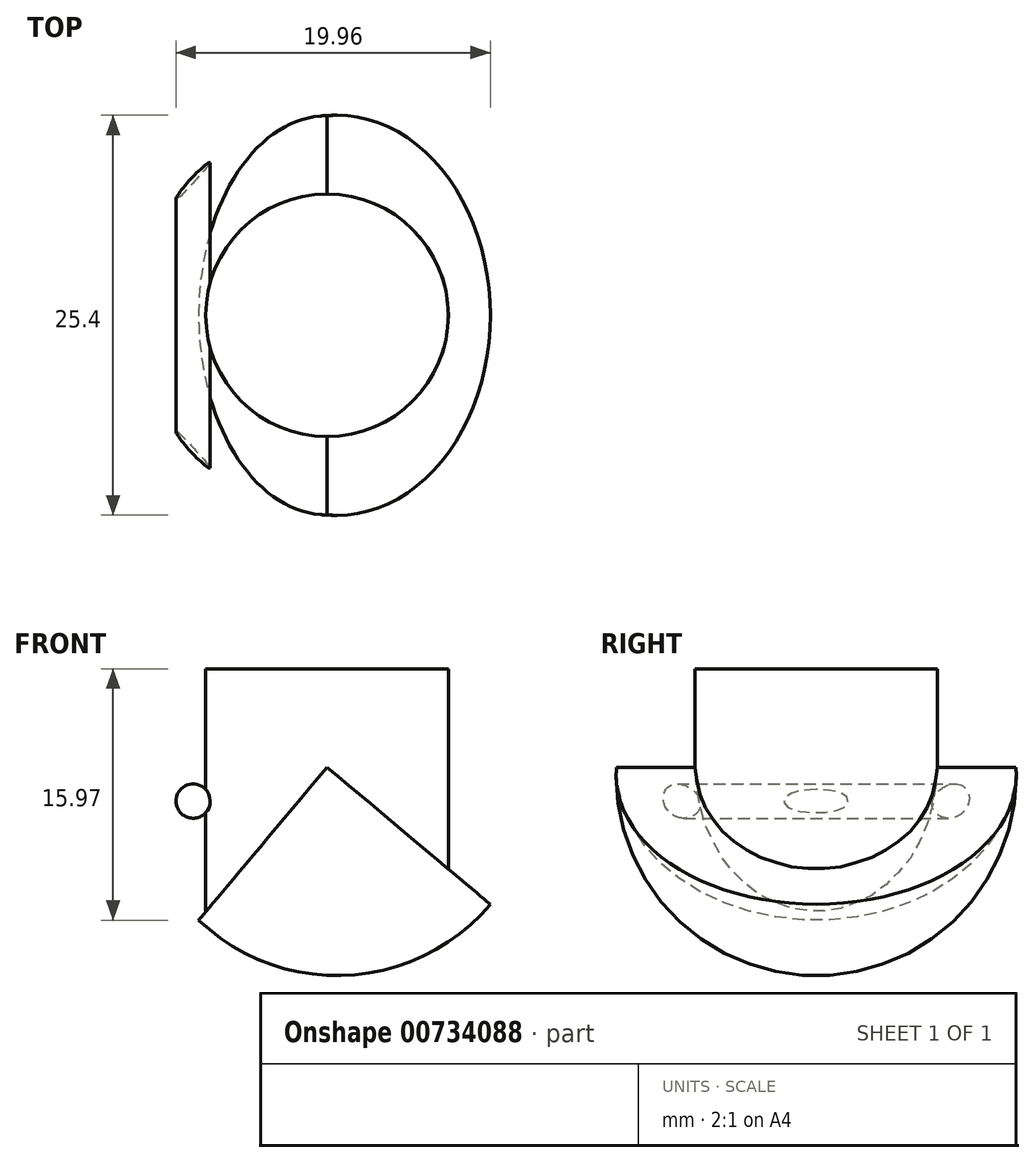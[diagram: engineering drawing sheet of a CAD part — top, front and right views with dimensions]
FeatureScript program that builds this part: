
annotation { "Feature Type Name" : "Feature", "Feature Type Description" : "" }
export const myFeature = defineFeature(function(context is Context, id is Id, definition is map)
    precondition{}
    {
        {
            var Q0;
            Q0=qCreatedBy(makeId("Top.planeOp"),FACE);
            var sketch = newSketch(context, id + "F0", { "sketchPlane" : qUnion([Q0])});
            skCircle(sketch, "E0", {"center": v(0, 0) * mm, "radius": 5.5 * mm});
            skSolve(sketch);
        }
        {
            var Q0;
            Q0=makeQuery(id+"F0.imprint","IMPRINT",FACE,{"disambiguationData":[TD([[makeQuery(id+"F0.imprint","IMPRINT",EDGE,{"derivedFrom":sQuery(id+"F0.wireOp",EDGE,"E0")}),1.0]])]});
            extrude(context, id + "F1", {"entities" : qUnion([Q0]), "depth" : 150 * mm, "offsetDistance" : 25 * mm});
        }
        {
            var Q0;
            Q0=makeQuery(id+"F1.opExtrude","CAP_FACE",FACE,{"disambiguationData":[OSD([sQuery(id+"F0.wireOp",EDGE,"E0")])],"isStart":false});
            var sketch = newSketch(context, id + "F2", { "sketchPlane" : qUnion([Q0])});
            skArc(sketch, "E1", {"start": v(-49.75, 2.8) * mm, "mid": v(-66.59, 8.91) * mm, "end": v(-77.27, -5.46) * mm});
            skLineSegment(sketch, "E2", {"start": v(-49.75, 2.8) * mm, "end": v(-59.49, -5.4) * mm});
            skPoint(sketch, "E3.orphan", {"position": v(-47.27, -5.46) * mm});
            skCircle(sketch, "E4", {"center": v(-60.28, 5.16) * mm, "radius": 2 * mm});
            skLineSegment(sketch, "E5", {"start": v(-53.08, 0) * mm, "end": v(-41.16, 0) * mm});
            skLineSegment(sketch, "E6.MirrorCS", {"start": v(-53.05, -10.77) * mm, "end": v(-41.13, -10.7) * mm});
            skLineSegment(sketch, "E7.MirrorCS", {"start": v(-49.7, -13.56) * mm, "end": v(-59.49, -5.4) * mm});
            skArc(sketch, "E8.MirrorCS", {"start": v(-49.7, -13.56) * mm, "mid": v(-66.5, -19.76) * mm, "end": v(-77.27, -5.46) * mm});
            skSolve(sketch);
        }
        {
            var Q0;
            Q0 = qSketchRegion(id + "F2", true);
            extrude(context, id + "F3", {"entities" : qUnion([Q0]), "depth" : 7 * mm, "offsetDistance" : 25 * mm});
        }
        {
            var Q0;
            Q0=qCreatedBy(makeId("Right.planeOp"),FACE);
            var sketch = newSketch(context, id + "F4", { "sketchPlane" : qUnion([Q0])});
            skLineSegment(sketch, "E9", {"start": v(0, 180.23) * mm, "end": v(0, 162.06) * mm});
            skArc(sketch, "E10", {"start": v(0, 162.06) * mm, "mid": v(9.07, 171.14) * mm, "end": v(0, 180.23) * mm});
            skSolve(sketch);
        }
        {
            var Q0;
            Q0=makeQuery(id+"F4.imprint","IMPRINT",FACE,{"disambiguationData":[TD([[makeQuery(id+"F4.imprint","IMPRINT",EDGE,{"derivedFrom":sQuery(id+"F4.wireOp",EDGE,"E9")}),1.0]])]});
            var Q1;
            Q1=sQuery(id+"F4.wireOp",EDGE,"E9");
            revolve(context, id + "F5", {"surfaceOperationType" : NewSurfaceOperationType.NEW, "entities" : qUnion([Q0]), "axis" : qUnion([Q1]), "revolveType" : RevolveType.FULL});
        }
        {
            var Q0;
            Q0=qCreatedBy(makeId("Right.planeOp"),FACE);
            var sketch = newSketch(context, id + "F6", { "sketchPlane" : qUnion([Q0])});
            skLineSegment(sketch, "E11.bottom", {"start": v(14.24, 171.73) * mm, "end": v(-11.17, 171.73) * mm});
            skLineSegment(sketch, "E11.top", {"start": v(14.24, 160.88) * mm, "end": v(-11.17, 160.88) * mm});
            skLineSegment(sketch, "E11.left", {"start": v(14.24, 171.73) * mm, "end": v(14.24, 160.88) * mm});
            skLineSegment(sketch, "E11.right", {"start": v(-11.17, 171.73) * mm, "end": v(-11.17, 160.88) * mm});
            skSolve(sketch);
        }
        {
            var Q0;
            Q0=makeQuery(id+"F6.imprint","IMPRINT",FACE,{"disambiguationData":[TD([[makeQuery(id+"F6.imprint","IMPRINT",EDGE,{"derivedFrom":sQuery(id+"F6.wireOp",EDGE,"E11.bottom")}),1.0]])]});
            extrude(context, id + "F7", {"entities" : qUnion([Q0]), "operationType" : NewBodyOperationType.REMOVE, "oppositeDirection" : true, "depth" : 10.7 * mm, "offsetDistance" : 25 * mm});
        }
        {
            var Q0;
            Q0=makeQuery(id+"F5.opRevolve","SWEPT_BODY",BODY,{"disambiguationData":[OSD([sQuery(id+"F4.wireOp",EDGE,"E9"),sQuery(id+"F4.wireOp",EDGE,"E10")])]});
            var Q1;
            Q1=makeQuery(id+"F7.boolean.opBoolean","COPY",EDGE,{"derivedFrom":makeQuery(id+"F7.opExtrude","CAP_EDGE",EDGE,{"disambiguationData":[OSD([sQuery(id+"F6.wireOp",EDGE,"E11.bottom")])],"isStart":true})});
            transform(context, id + "F8", {"entities" : qUnion([Q0]), "transformType" : TransformType.ROTATION, "transformAxis" : qUnion([Q1]), "angle" : 50 * degree, "makeCopy" : false});
        }
        {
            var Q0;
            Q0=qCreatedBy(makeId("Front.planeOp"),FACE);
            var sketch = newSketch(context, id + "F9", { "sketchPlane" : qUnion([Q0])});
            skCircle(sketch, "E12", {"center": v(-6.08, 170.2) * mm, "radius": 0.78 * mm});
            skSolve(sketch);
        }
        {
            var Q0;
            Q0 = qSketchRegion(id + "F9", true);
            var Q1;
            Q1=sQuery(id+"F9.wireOp",EDGE,"E12");
            extrude(context, id + "F10", {"entities" : qUnion([Q0]), "operationType" : NewBodyOperationType.REMOVE, "surfaceEntities" : qUnion([Q1]), "depth" : 25 * mm, "offsetDistance" : 25 * mm, "hasSecondDirection" : true, "secondDirectionOppositeDirection" : true, "secondDirectionDepth" : 25 * mm});
        }
        {
            var Q0;
            Q0=makeQuery(id+"F1.opExtrude","SWEPT_BODY",BODY,{"disambiguationData":[OSD([sQuery(id+"F0.wireOp",EDGE,"E0")])]});
            var Q1;
            Q1=qCreatedBy(makeId("Origin.pointOp"),VERTEX);
            transform(context, id + "F11", {"entities" : qUnion([Q0]), "transformType" : TransformType.TRANSLATION_3D, "dx" : 0 * mm, "dy" : 0 * mm, "dz" : 24.7 * mm, "makeCopy" : false});
        }
        {
            var Q0;
            Q0=makeQuery(id+"F1.opExtrude","SWEPT_BODY",BODY,{"disambiguationData":[OSD([sQuery(id+"F0.wireOp",EDGE,"E0")])]});
            var Q1;
            Q1=makeQuery(id+"F5.opRevolve","SWEPT_BODY",BODY,{"disambiguationData":[OSD([sQuery(id+"F4.wireOp",EDGE,"E9"),sQuery(id+"F4.wireOp",EDGE,"E10")])]});
            booleanBodies(context, id + "F12", {"operationType" : BooleanOperationType.SUBTRACTION, "tools" : qUnion([Q0]), "targets" : qUnion([Q1])});
        }
        {
            var Q0;
            Q0=makeQuery(id+"F3.opExtrude","SWEPT_BODY",BODY,{"disambiguationData":[OSD([sQuery(id+"F2.wireOp",EDGE,"E1"),sQuery(id+"F2.wireOp",EDGE,"E2"),sQuery(id+"F2.wireOp",EDGE,"E4"),sQuery(id+"F2.wireOp",EDGE,"E7.MirrorCS"),sQuery(id+"F2.wireOp",EDGE,"E8.MirrorCS")])]});
            deleteBodies(context, id + "F13", {"entities" : qUnion([Q0])});
        }
        {
            var Q0;
            Q0=makeQuery(id+"F12.opBoolean","COPY",FACE,{"derivedFrom":makeQuery(id+"F1.opExtrude","CAP_FACE",FACE,{"disambiguationData":[OSD([sQuery(id+"F0.wireOp",EDGE,"E0")])],"isStart":false})});
            extrude(context, id + "F14", {"entities" : qUnion([Q0]), "operationType" : NewBodyOperationType.REMOVE, "oppositeDirection" : true, "depth" : 1.5 * mm, "offsetDistance" : 25 * mm});
        }
        {
            var Q0;
            Q0=makeQuery(id+"F5.opRevolve","SWEPT_BODY",BODY,{"disambiguationData":[OSD([sQuery(id+"F4.wireOp",EDGE,"E9"),sQuery(id+"F4.wireOp",EDGE,"E10")])]});
            var Q1;
            Q1=qCreatedBy(makeId("Origin.pointOp"),VERTEX);
            var Q2;
            Q2=qCreatedBy(makeId("Origin.pointOp"),VERTEX);
            transform(context, id + "F15", {"entities" : qUnion([Q0]), "transformType" : TransformType.SCALE_UNIFORMLY, "scale" : 1.4, "scalePoint" : qUnion([Q2]), "makeCopy" : false});
        }
    });
